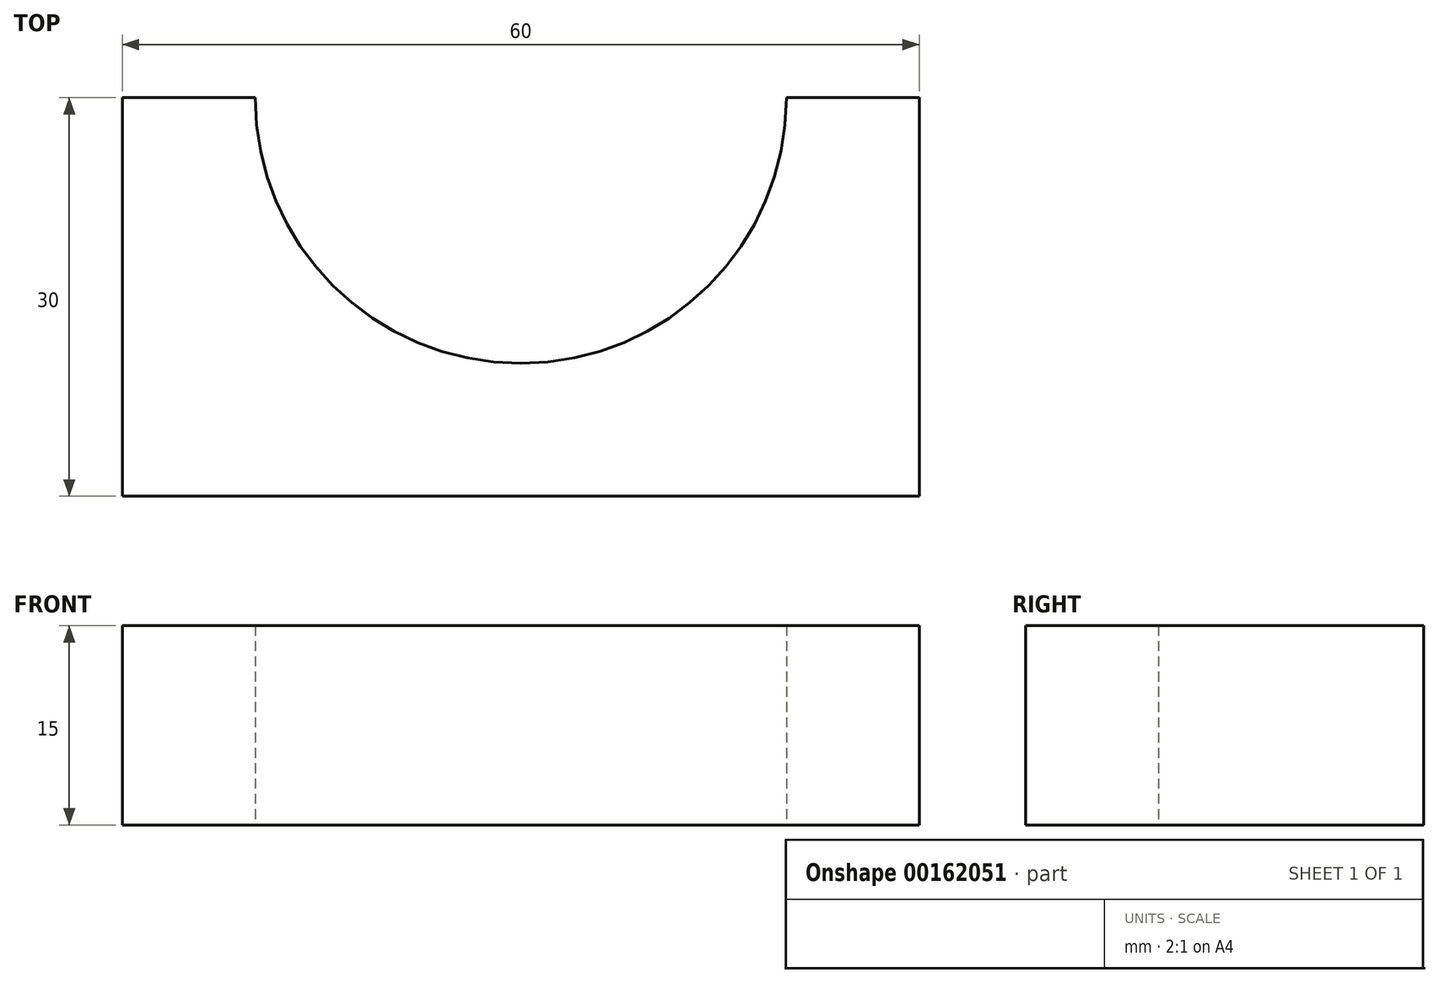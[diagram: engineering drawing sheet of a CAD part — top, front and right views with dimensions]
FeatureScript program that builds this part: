
annotation { "Feature Type Name" : "Feature", "Feature Type Description" : "" }
export const myFeature = defineFeature(function(context is Context, id is Id, definition is map)
    precondition{}
    {
        {
            var Q0;
            Q0=qCreatedBy(makeId("Top.planeOp"),FACE);
            var sketch = newSketch(context, id + "F0", { "sketchPlane" : qUnion([Q0])});
            skLineSegment(sketch, "E0", {"start": v(0, 0) * mm, "end": v(-30, 0) * mm});
            skLineSegment(sketch, "E1", {"start": v(-30, 0) * mm, "end": v(-30, 30) * mm});
            skLineSegment(sketch, "E2", {"start": v(-30, 30) * mm, "end": v(-20, 30) * mm});
            skArc(sketch, "E3", {"start": v(-20, 30) * mm, "mid": v(-14.14, 15.86) * mm, "end": v(0, 10) * mm});
            skArc(sketch, "E4.MirrorCS", {"start": v(20, 30) * mm, "mid": v(14.14, 15.86) * mm, "end": v(0, 10) * mm});
            skLineSegment(sketch, "E5.MirrorCS", {"start": v(30, 30) * mm, "end": v(20, 30) * mm});
            skLineSegment(sketch, "E6.MirrorCS", {"start": v(30, 0) * mm, "end": v(30, 30) * mm});
            skLineSegment(sketch, "E7.MirrorCS", {"start": v(0, 0) * mm, "end": v(30, 0) * mm});
            skSolve(sketch);
        }
        {
            var Q0;
            Q0=makeQuery(id+"F0.imprint","IMPRINT",FACE,{"disambiguationData":[TD([[makeQuery(id+"F0.imprint","IMPRINT",EDGE,{"derivedFrom":sQuery(id+"F0.wireOp",EDGE,"E0")}),-1.0]])]});
            extrude(context, id + "F1", {"entities" : qUnion([Q0]), "depth" : 15 * mm});
        }
    });
